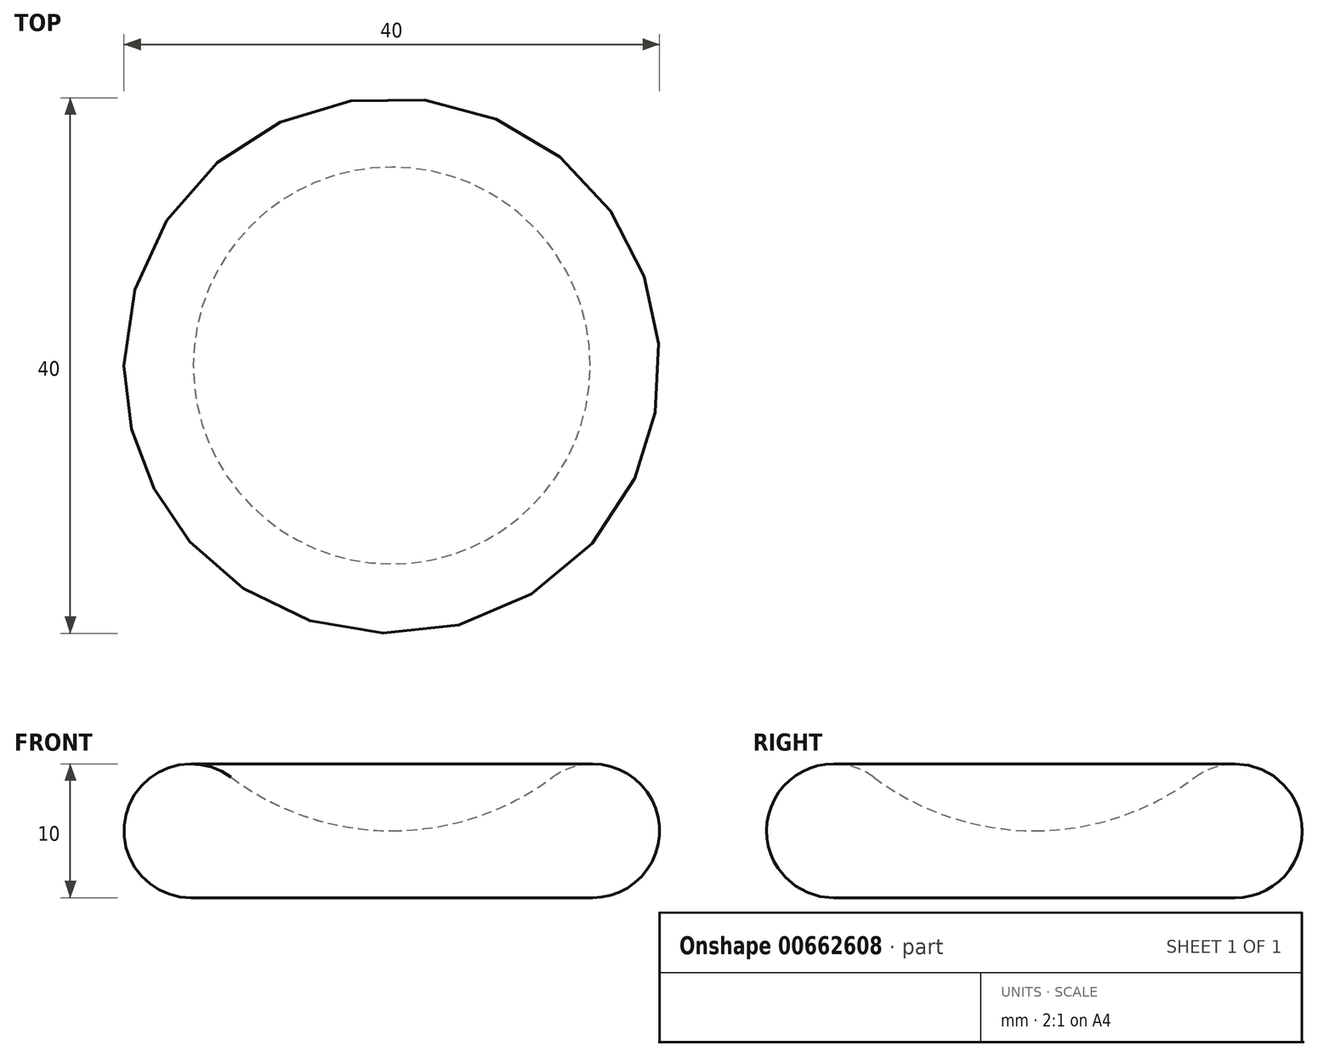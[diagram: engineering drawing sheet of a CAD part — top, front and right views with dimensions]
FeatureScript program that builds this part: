
annotation { "Feature Type Name" : "Feature", "Feature Type Description" : "" }
export const myFeature = defineFeature(function(context is Context, id is Id, definition is map)
    precondition{}
    {
        {
            var Q0;
            Q0=qCreatedBy(makeId("Front.planeOp"),FACE);
            var sketch = newSketch(context, id + "F0", { "sketchPlane" : qUnion([Q0])});
            skArc(sketch, "E0", {"start": v(-12, 9) * mm, "mid": v(-19.77, 6.5) * mm, "end": v(-14.82, 0) * mm});
            skArc(sketch, "E1", {"start": v(-12, 9) * mm, "mid": v(-6.32, 6.03) * mm, "end": v(0, 5) * mm});
            skLineSegment(sketch, "E2", {"start": v(-14.82, 0) * mm, "end": v(0, 0) * mm});
            skLineSegment(sketch, "E3", {"start": v(0, 0) * mm, "end": v(0, 5) * mm});
            skSolve(sketch);
        }
        {
            var Q0;
            Q0=makeQuery(id+"F0.imprint","IMPRINT",FACE,{"disambiguationData":[TD([[makeQuery(id+"F0.imprint","IMPRINT",EDGE,{"derivedFrom":sQuery(id+"F0.wireOp",EDGE,"E0")}),1.0]])]});
            var Q1;
            Q1=sQuery(id+"F0.wireOp",EDGE,"E3");
            revolve(context, id + "F1", {"entities" : qUnion([Q0]), "axis" : qUnion([Q1]), "revolveType" : RevolveType.FULL});
        }
    });
